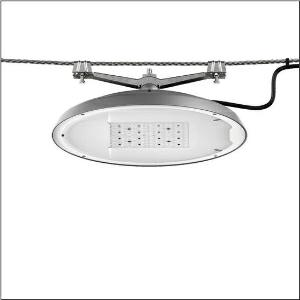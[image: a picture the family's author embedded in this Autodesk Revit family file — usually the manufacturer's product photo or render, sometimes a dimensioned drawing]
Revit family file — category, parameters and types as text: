
# Revit family: dl_50_iq_mini___st0_8s_5xa248v31f08me_c7b8
name_source: partatom
category: Lighting Fixtures
units: mm (PartAtom-declared; Revit-internal decimal feet)

## family parameters
Cut with Voids When Loaded = No
Host = Face
Light Source = No
Part Type = Normal
Room Calculation Point = No
Round Connector Dimension = Use Diameter
Shared = No

## types (1)
- --- (1 x LED, 15660 lm, 107.8 W, 3000K)
    Apparent Load = 108 VA
    CIE Flux Codes = 38 75 97 100 100
    Color Rendering = 70
    Color Temperature = 3000K
    Default Elevation = 1800 mm
    Description = DL 50 iQ mini, catenary luminaire, primary light control with lens, of PMMA, primary optical cover: cover, of toughened safety glass, transparent, light distribution: ST0.8s, light emission: direct distribution, primary light characteristic: symmetric, installation type: suspended mounting, LED, High Power LED, rated luminous flux: 15.660lm, luminous efficacy: 145lm/W, light colour: 730, colour temperature: 3000K, control gear: iQ Street-Remote, control: optimised constant luminous flux control (CLO 2.0), Desk-Remote (wireless, voltage-free reading and setting of iQ features in the workshop via application-optimized NFC function/RFID function), Light-Fading, Smart-Wire, Night-Set, Lumen-Switch, Temp-Guard, Auto-Match, Street-Remote, mains connection: 230..240V, AC, 50/60Hz, start of lifetime: 108W, end of service life: 118W, reduction: 47W, luminaire housing, of diecast aluminium, powder-coated, SITECO metallic grey (DB 702S), diameter: 500mm, height: 115mm, mounting height: 4..12m, protection rating (complete): IP66, insulation class (complete): insulation class II (safety insulation), certification: CE, ENEC, ENEC+, VDE, impact resistance: IK08, permissible operating ambient temperature for outdoor applications: -25..+40°C, standard-compliant lighting for roads and squares, packaging unit: 1 piece

Light Distribution: ST0.8s
    Height = 124 mm  [stored 0.406824 ft]
    Lamp = 1 x LED
    Lamp Light Flux = 15660 lm
    Lamp Power = 107.8 W
    Lamp count = 1
    Length = 500 mm
    Luminous efficacy = 145 lm/W
    Manufacturer = Siteco
    ModVariant = No
    Model = 5XA248V31F08ME
    Number of Poles = 1
    OnlyDefault = Yes
    Power Factor = 1
    Product Name = DL 50 iQ mini | ST0.8s
    Product group = catenary luminaire
    ProductGroupID = 6300
    Protection Class = Protection class II
    Protection Degree = IP 66
    RLX_Detail_Level = 1
    RLX_Emergency_Light_Flux = 0 lm
    RLX_Emergency_Type = 0
    RLX_Emergency_Type_DB = No
    RlxData = <blob elided: 127477 chars, md5=ce0e5f0f>
    Socket = socket
    Standby Power = 0 W
    System Light Flux = 15660 lm
    System Power = 108 W
    Type Comments = factory setting: luminous flux: 100 % | dim-lin: 254 | 565 mA
    Type Image = l_1251783.jpg
    URL = http://relux.com
    VarID = @adj_142033
    Voltage = 0 V
    Weight = 0.00 kg
    Width = 0 mm  [stored 0 ft]

note: [stored X ft] marks values corroborated as IEEE doubles in the binary element streams (Revit-internal decimal feet)

## geometry (parser evidence)
native form markers: Blend x4, Sweep x16
no freeform markers — native parametric forms only
